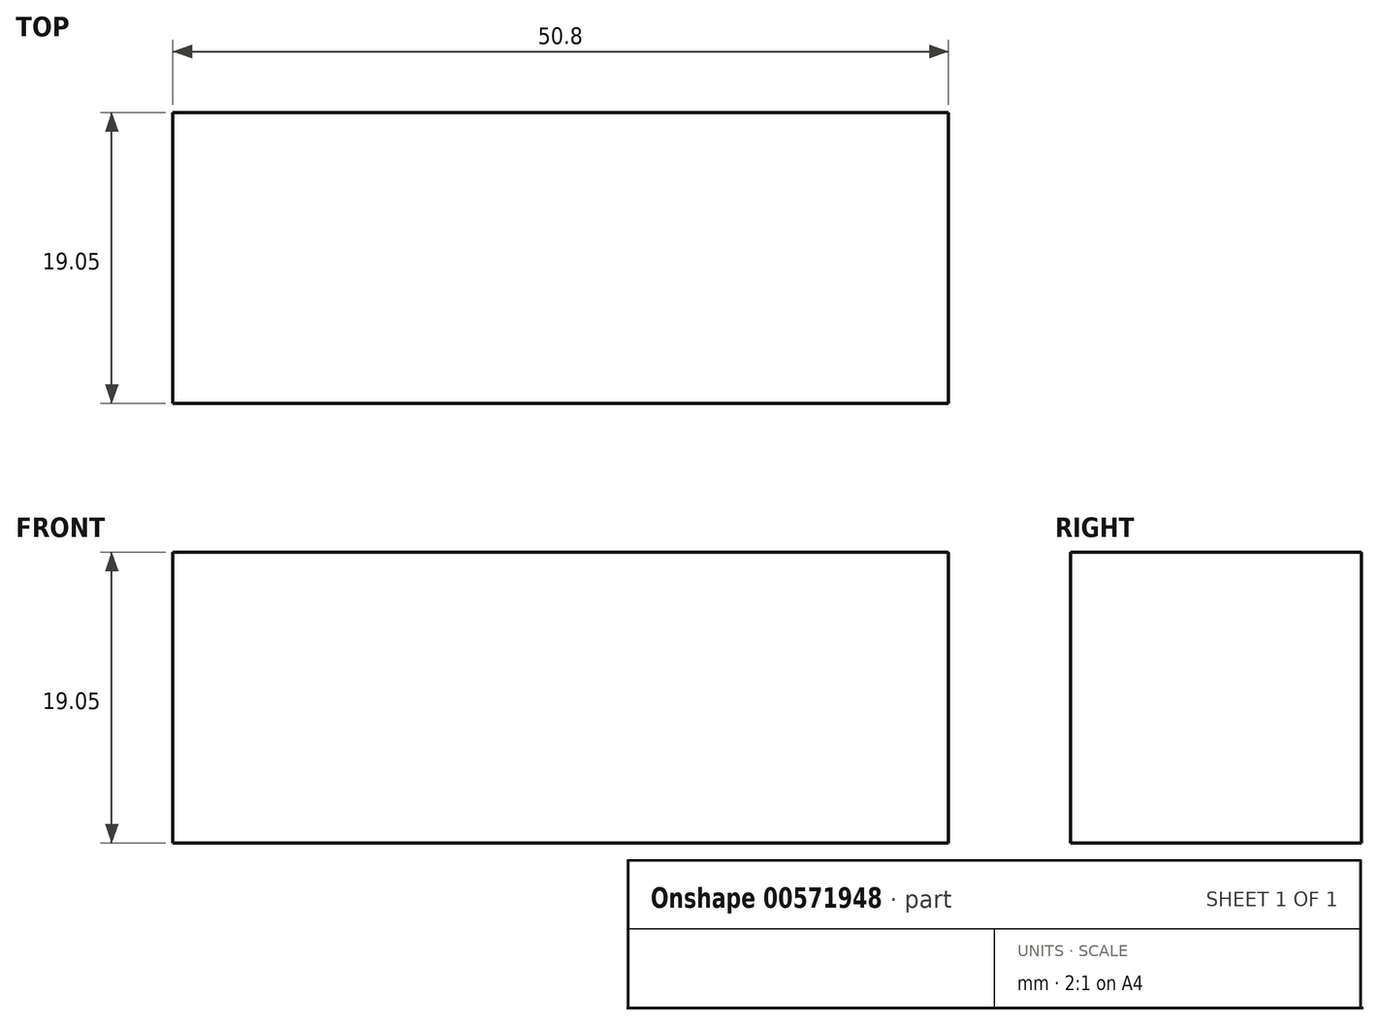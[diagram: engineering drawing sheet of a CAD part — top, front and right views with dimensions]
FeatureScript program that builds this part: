
annotation { "Feature Type Name" : "Feature", "Feature Type Description" : "" }
export const myFeature = defineFeature(function(context is Context, id is Id, definition is map)
    precondition{}
    {
        {
            var Q0;
            Q0=qCreatedBy(makeId("Top.planeOp"),FACE);
            var sketch = newSketch(context, id + "F0", { "sketchPlane" : qUnion([Q0])});
            skLineSegment(sketch, "E0.bottom", {"start": v(0, 0) * mm, "end": v(-50.8, 0) * mm});
            skLineSegment(sketch, "E0.top", {"start": v(0, -19.05) * mm, "end": v(-50.8, -19.05) * mm});
            skLineSegment(sketch, "E0.left", {"start": v(0, 0) * mm, "end": v(0, -19.05) * mm});
            skLineSegment(sketch, "E0.right", {"start": v(-50.8, 0) * mm, "end": v(-50.8, -19.05) * mm});
            skSolve(sketch);
        }
        {
            var Q0;
            Q0 = qSketchRegion(id + "F0", true);
            extrude(context, id + "F1", {"entities" : qUnion([Q0]), "depth" : 19.05 * mm, "offsetDistance" : 25.4 * mm});
        }
    });
